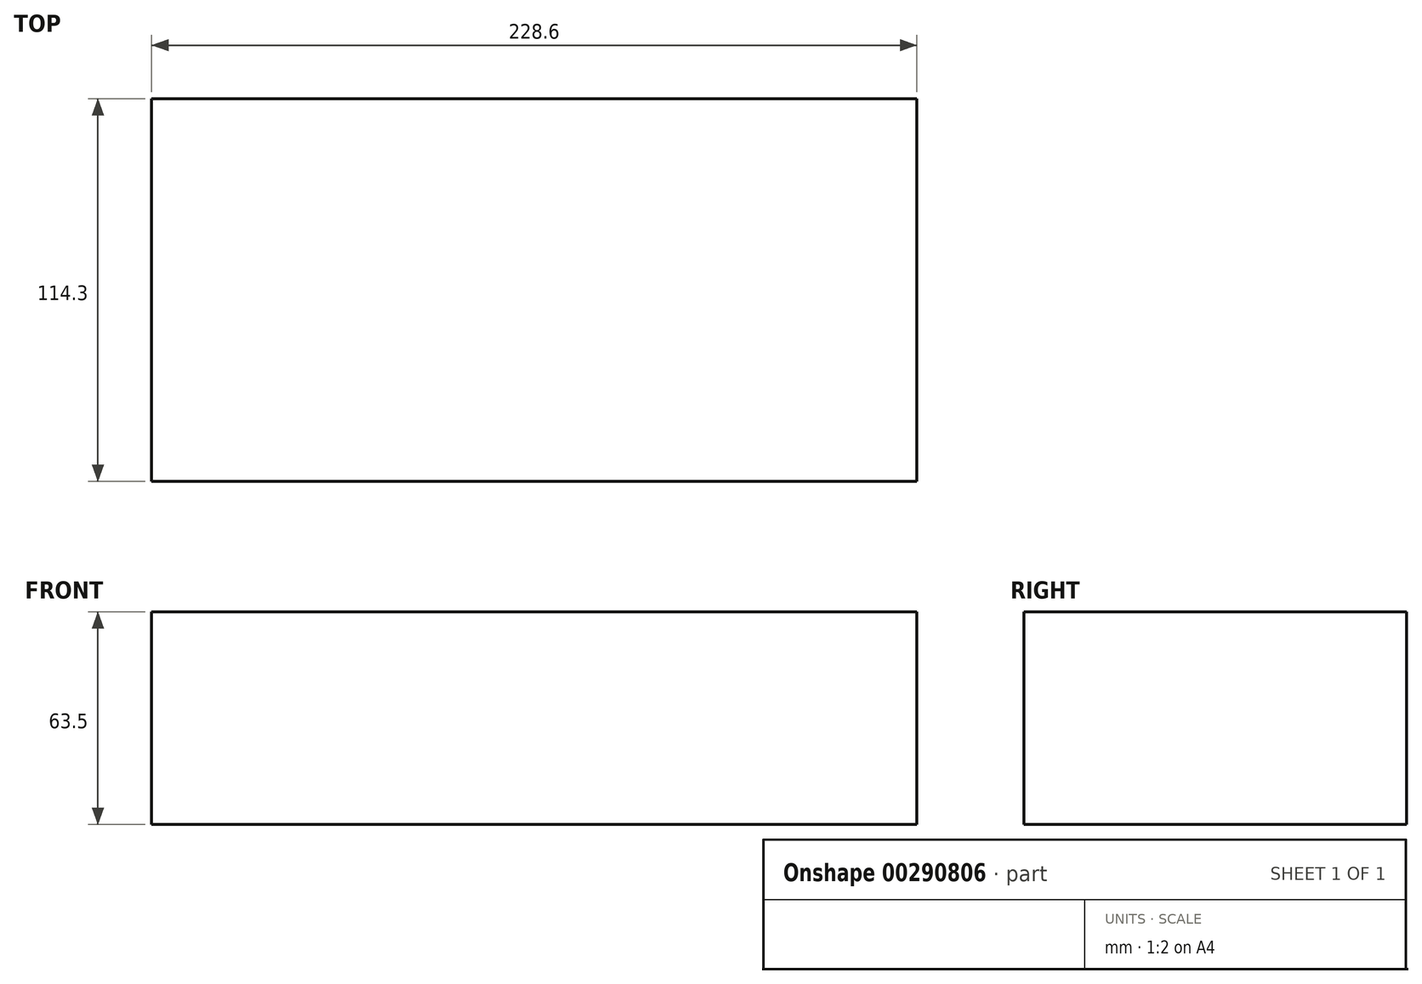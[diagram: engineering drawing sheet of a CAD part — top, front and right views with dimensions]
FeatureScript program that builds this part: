
annotation { "Feature Type Name" : "Feature", "Feature Type Description" : "" }
export const myFeature = defineFeature(function(context is Context, id is Id, definition is map)
    precondition{}
    {
        {
            var Q0;
            Q0=qCreatedBy(makeId("Top.planeOp"),FACE);
            var sketch = newSketch(context, id + "F0", { "sketchPlane" : qUnion([Q0])});
            skLineSegment(sketch, "E0.bottom", {"start": v(-114.3, 0) * mm, "end": v(114.3, 0) * mm});
            skLineSegment(sketch, "E0.top", {"start": v(-114.3, -114.3) * mm, "end": v(114.3, -114.3) * mm});
            skLineSegment(sketch, "E0.left", {"start": v(-114.3, 0) * mm, "end": v(-114.3, -114.3) * mm});
            skLineSegment(sketch, "E0.right", {"start": v(114.3, 0) * mm, "end": v(114.3, -114.3) * mm});
            skSolve(sketch);
        }
        {
            var Q0;
            Q0 = qSketchRegion(id + "F0", true);
            extrude(context, id + "F1", {"entities" : qUnion([Q0]), "oppositeDirection" : true, "depth" : 63.5 * mm});
        }
    });
